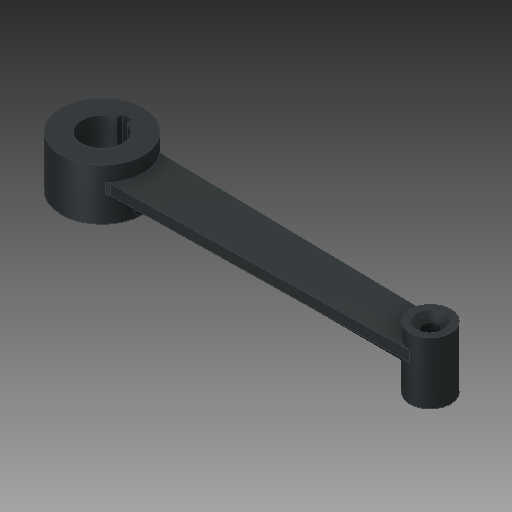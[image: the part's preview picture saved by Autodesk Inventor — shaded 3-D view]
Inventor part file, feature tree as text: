
AUTODESK INVENTOR PART (.ipt)
format: ipt  version: 2020 (Build 240168000, 168)  size: 192,512 bytes
history: native  units: in
note: dims shown in document units (in); Inventor stores cm internally (conversion verified against a paired STEP export)
features: extrude x5, sketch x5, fillet x2, hole x2, projected_geometry x1
ambient origin geometry x8: Origin, YZ Plane, XZ Plane, XY Plane, X Axis, Y Axis, Z Axis, Center Point
bodies: Solid1 (feature_tree)
feature tree (15):
  extrude  "Extrusion1"  Depth=1.0in
  extrude  "Extrusion2"  Depth=0.625in
  extrude  "Extrusion3"  TaperAngle=0.0deg  [1 undecoded]
  extrude  "Extrusion4"  Depth=0.125in TaperAngle=0.0deg
  fillet  "Fillet1"  Radius=0.0625in
  fillet  "Fillet2"  Radius=0.0625in
  hole  "Hole1"  [1 undecoded]
  hole  "Hole2"  [1 undecoded]
  extrude  "Extrusion5"  Depth=0.0625in
  sketch  "Sketch1"  dims[d0=4.0in d1=1.0in]
  sketch  "Sketch2"  dims[d2=0.5in d3=0.625in]
  sketch  "Sketch3"  dims[d4=0.3125in d5=0.0in]
  projected_geometry  "Projected Loop1"
  sketch  "Sketch4"  dims[d6=0.125in d7=0.0in d8=0.1875in d9=0.4375in d10=0.0in d11=0.0in]
  sketch  "Sketch5"  dims[d12=0.1875in d13=0.5625in d14=0.0in d15=0.0in d16=0.0625in d17=0.0625in d18=0.25in d19=0.0in d20=0.0625in d21=1.0in d22=1.0in d23=0.5in d24=0.75in d25=0.375in d26=0.25in d27=0.5635in d28=1.0in d29=0.8108in d30=1.0in d31=1.0in d32=0.1875in d33=0.75in d34=0.3438in d35=0.25in d36=90.0deg d37=1.0in d38=0.8108in d39=0.125in d40=0.0625in d41=0.0625in d42=1.0in d43=0.0in]
note: 3 required parameter values undecoded (feature->parameter linkage not recoverable at this tier; creation-order binding heuristic only, values carry confidence <= 0.55)
